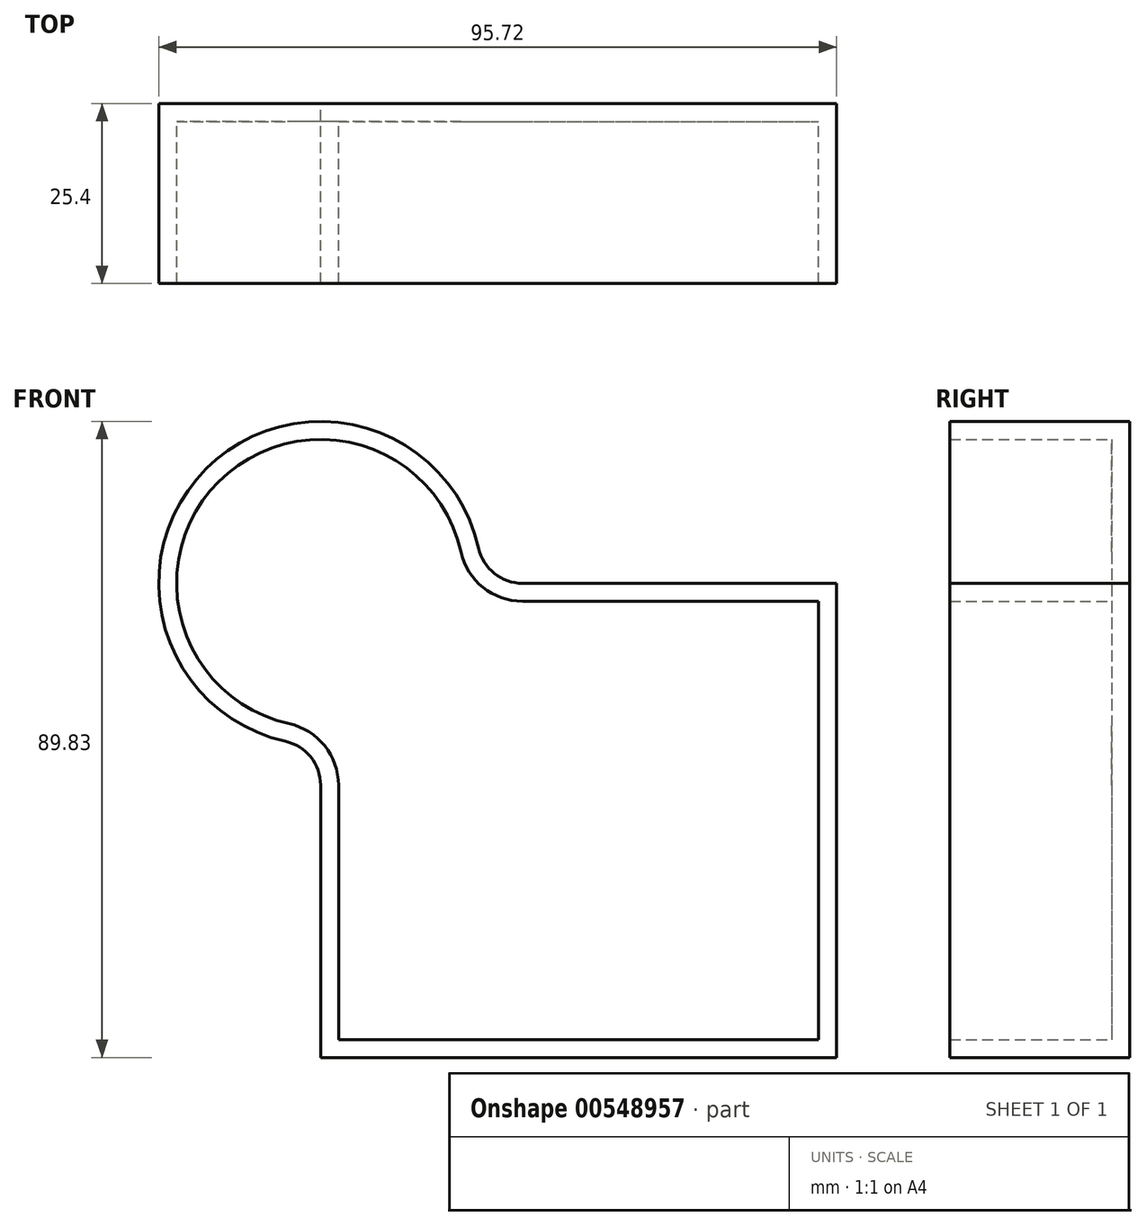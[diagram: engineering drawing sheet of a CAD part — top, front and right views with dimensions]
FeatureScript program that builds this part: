
annotation { "Feature Type Name" : "Feature", "Feature Type Description" : "" }
export const myFeature = defineFeature(function(context is Context, id is Id, definition is map)
    precondition{}
    {
        {
            var Q0;
            Q0=qCreatedBy(makeId("Front.planeOp"),FACE);
            var sketch = newSketch(context, id + "F0", { "sketchPlane" : qUnion([Q0])});
            skLineSegment(sketch, "E0.bottom", {"start": v(-6.93, 34.24) * mm, "end": v(37.42, 34.24) * mm});
            skLineSegment(sketch, "E0.top", {"start": v(-35.44, -32.73) * mm, "end": v(37.42, -32.73) * mm});
            skLineSegment(sketch, "E0.left", {"start": v(-35.44, 5.73) * mm, "end": v(-35.44, -32.73) * mm});
            skLineSegment(sketch, "E0.right", {"start": v(37.42, 34.24) * mm, "end": v(37.42, -32.73) * mm});
            skArc(sketch, "E1", {"start": v(-13.12, 39.2) * mm, "mid": v(-51.6, 50.4) * mm, "end": v(-40.4, 11.92) * mm});
            skPoint(sketch, "E2.visualSharp", {"position": v(-12.58, 34.24) * mm});
            skArc(sketch, "E2.filletArc", {"start": v(-13.12, 39.2) * mm, "mid": v(-10.9, 35.64) * mm, "end": v(-6.93, 34.24) * mm});
            skPoint(sketch, "E3.visualSharp", {"position": v(-35.44, 11.38) * mm});
            skArc(sketch, "E3.filletArc", {"start": v(-35.44, 5.73) * mm, "mid": v(-36.83, 9.7) * mm, "end": v(-40.4, 11.92) * mm});
            skSolve(sketch);
        }
        {
            var Q0;
            Q0 = qSketchRegion(id + "F0", true);
            extrude(context, id + "F1", {"entities" : qUnion([Q0]), "depth" : 25.4 * mm, "offsetDistance" : 25.4 * mm});
        }
        {
            var Q0;
            Q0=makeQuery(id+"F1.opExtrude","CAP_FACE",FACE,{"disambiguationData":[OSD([sQuery(id+"F0.wireOp",EDGE,"E0.bottom"),sQuery(id+"F0.wireOp",EDGE,"E0.top"),sQuery(id+"F0.wireOp",EDGE,"E0.left"),sQuery(id+"F0.wireOp",EDGE,"E0.right"),sQuery(id+"F0.wireOp",EDGE,"E1"),sQuery(id+"F0.wireOp",EDGE,"E2.filletArc"),sQuery(id+"F0.wireOp",EDGE,"E3.filletArc")])],"isStart":false});
            var sketch = newSketch(context, id + "F2", { "sketchPlane" : qUnion([Q0])});
            skFitSpline(sketch, "E4", {"points": [v(39.43, 34.24) * mm, v(58.12, 46.7) * mm, v(88.57, 40.15) * mm, v(113.46, 17.47) * mm, v(113.9, 13.47) * mm, v(61.66, 10.98) * mm, v(108.71, -11.93) * mm], "startDerivative": vector(116.04, 109.05) * mm, "endDerivative": vector(361.13, -133.52) * mm});
            skSolve(sketch);
        }
        {
            var Q0;
            Q0=makeQuery(id+"F1.opExtrude","CAP_FACE",FACE,{"disambiguationData":[OSD([sQuery(id+"F0.wireOp",EDGE,"E0.bottom"),sQuery(id+"F0.wireOp",EDGE,"E0.top"),sQuery(id+"F0.wireOp",EDGE,"E0.left"),sQuery(id+"F0.wireOp",EDGE,"E0.right"),sQuery(id+"F0.wireOp",EDGE,"E1"),sQuery(id+"F0.wireOp",EDGE,"E2.filletArc"),sQuery(id+"F0.wireOp",EDGE,"E3.filletArc")])],"isStart":false});
            shell(context, id + "F3", {"entities" : qUnion([Q0]), "thickness" : 2.54 * mm});
        }
    });
